# Revit family: 24100XXX__
name_source: partatom
category: Plumbing Fixtures
revit_build: Autodesk Revit 2018 (Build: 20170223_1515(x64)
units: mm (PartAtom-declared; Revit-internal decimal feet)

## family parameters
Always vertical = No
Cut with Voids When Loaded = No
OmniClass Number = 23.45.00.00
OmniClass Title = Sanitary, Laundry, and Cleaning Equipment
Part Type = Normal
Room Calculation Point = No
Round Connector Dimension = Use Diameter
Shared = No
Work Plane-Based = No

## types (3) — shared parameters
Always visible = Yes
BIMobject category = Showers
Design country = Germany
EAN code = 4059625315897
Edition number = 1
IFC Classification = Sanitary Terminal
Installation instructions = https://www.hansgrohe.com
Manufacturer country = Germany
Manufacturer name = hansgrohe
Material 1 = Hansgrohe - Pulsify - Graphite
Material main = Chrome
Product Guid = fa094d7f-457c-460f-ba76-47f1699f6a59
Product SKU = 24100XXX
Product data url = https://www.bimobject.com
Product family = Pulsify Select
Product group = Hand showers
Product name = 24100XXX Pulsify Select Hand shower 105 3jet Activation
Product url = https://www.hansgrohe.com
QR code = https://www.bimobject.com
Technical description = https://www.hansgrohe.com

## per-type parameters (varying)
| type | Material 2 |
| 000 Chrome | Hansgrohe - Pulsify - 000 Chrome |
| 670 Matte Black | Hansgrohe - Pulsify - 670 Matte Black |
| 700 Matt White | Hansgrohe - Pulsify - 700 Matt White |

## geometry (parser evidence)
native form markers: Sweep x3
no freeform markers — native parametric forms only
